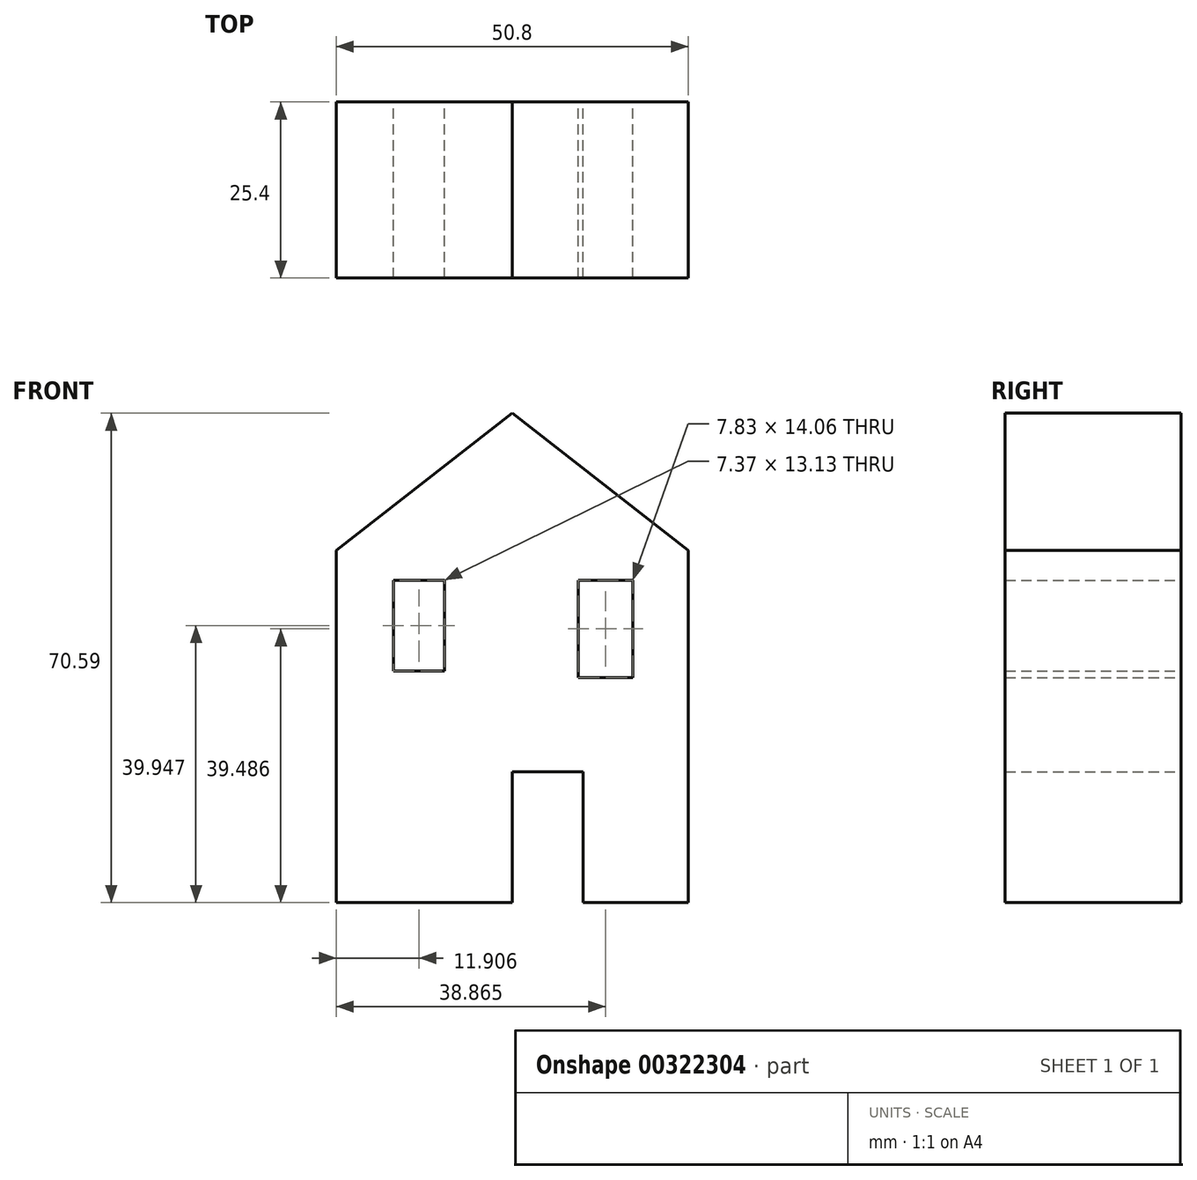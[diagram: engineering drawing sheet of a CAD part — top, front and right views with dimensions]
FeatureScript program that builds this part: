
annotation { "Feature Type Name" : "Feature", "Feature Type Description" : "" }
export const myFeature = defineFeature(function(context is Context, id is Id, definition is map)
    precondition{}
    {
        {
            var Q0;
            Q0=qCreatedBy(makeId("Front.planeOp"),FACE);
            var sketch = newSketch(context, id + "F0", { "sketchPlane" : qUnion([Q0])});
            skLineSegment(sketch, "E0.bottom", {"start": v(25.4, 25.4) * mm, "end": v(-25.4, 25.4) * mm});
            skLineSegment(sketch, "E0.top", {"start": v(25.4, -25.4) * mm, "end": v(-25.4, -25.4) * mm});
            skLineSegment(sketch, "E0.left", {"start": v(25.4, 25.4) * mm, "end": v(25.4, -25.4) * mm});
            skLineSegment(sketch, "E0.right", {"start": v(-25.4, 25.4) * mm, "end": v(-25.4, -25.4) * mm});
            skPoint(sketch, "E0.middle", {"position": v(0, 0) * mm});
            skLineSegment(sketch, "E1", {"start": v(-25.4, 25.4) * mm, "end": v(0, 45.2) * mm});
            skLineSegment(sketch, "E2", {"start": v(0, 45.2) * mm, "end": v(25.4, 25.4) * mm});
            skLineSegment(sketch, "E3.bottom", {"start": v(0, -25.4) * mm, "end": v(10.24, -25.4) * mm});
            skLineSegment(sketch, "E3.top", {"start": v(0, -6.54) * mm, "end": v(10.24, -6.54) * mm});
            skLineSegment(sketch, "E3.left", {"start": v(0, -25.4) * mm, "end": v(0, -6.54) * mm});
            skLineSegment(sketch, "E3.right", {"start": v(10.24, -25.4) * mm, "end": v(10.24, -6.54) * mm});
            skCircle(sketch, "E4", {"center": v(7.94, -16.21) * mm, "radius": 2.3 * mm});
            skLineSegment(sketch, "E5.bottom", {"start": v(-17.18, 7.98) * mm, "end": v(-9.8, 7.98) * mm});
            skLineSegment(sketch, "E5.top", {"start": v(-17.18, 21.11) * mm, "end": v(-9.8, 21.11) * mm});
            skLineSegment(sketch, "E5.left", {"start": v(-17.18, 7.98) * mm, "end": v(-17.18, 21.11) * mm});
            skLineSegment(sketch, "E5.right", {"start": v(-9.8, 7.98) * mm, "end": v(-9.8, 21.11) * mm});
            skLineSegment(sketch, "E6.bottom", {"start": v(9.55, 7.06) * mm, "end": v(17.38, 7.06) * mm});
            skLineSegment(sketch, "E6.top", {"start": v(9.55, 21.11) * mm, "end": v(17.38, 21.11) * mm});
            skLineSegment(sketch, "E6.left", {"start": v(9.55, 7.06) * mm, "end": v(9.55, 21.11) * mm});
            skLineSegment(sketch, "E6.right", {"start": v(17.38, 7.06) * mm, "end": v(17.38, 21.11) * mm});
            skLineSegment(sketch, "E7", {"start": v(-17.18, 14.55) * mm, "end": v(-9.8, 14.55) * mm});
            skLineSegment(sketch, "E8", {"start": v(-13.5, 21.11) * mm, "end": v(-13.5, 7.98) * mm});
            skLineSegment(sketch, "E9", {"start": v(9.55, 14.09) * mm, "end": v(20.15, 14.09) * mm});
            skPoint(sketch, "E9.endSnap0", {"position": v(17.38, 14.09) * mm});
            skLineSegment(sketch, "E10", {"start": v(13.47, 21.11) * mm, "end": v(13.47, 7.06) * mm});
            skSolve(sketch);
        }
        {
            var Q0;
            Q0=makeQuery(id+"F0.imprint","IMPRINT",FACE,{"disambiguationData":[TD([[makeQuery(id+"F0.imprint","IMPRINT",EDGE,{"derivedFrom":sQuery(id+"F0.wireOp",EDGE,"E0.bottom")}),1.0]])]});
            var Q1;
            Q1=makeQuery(id+"F0.imprint","IMPRINT",FACE,{"disambiguationData":[TD([[makeQuery(id+"F0.imprint","IMPRINT",EDGE,{"derivedFrom":sQuery(id+"F0.wireOp",EDGE,"E0.bottom")}),-1.0]])]});
            extrude(context, id + "F1", {"entities" : qUnion([Q0, Q1]), "depth" : 25.4 * mm});
        }
    });
